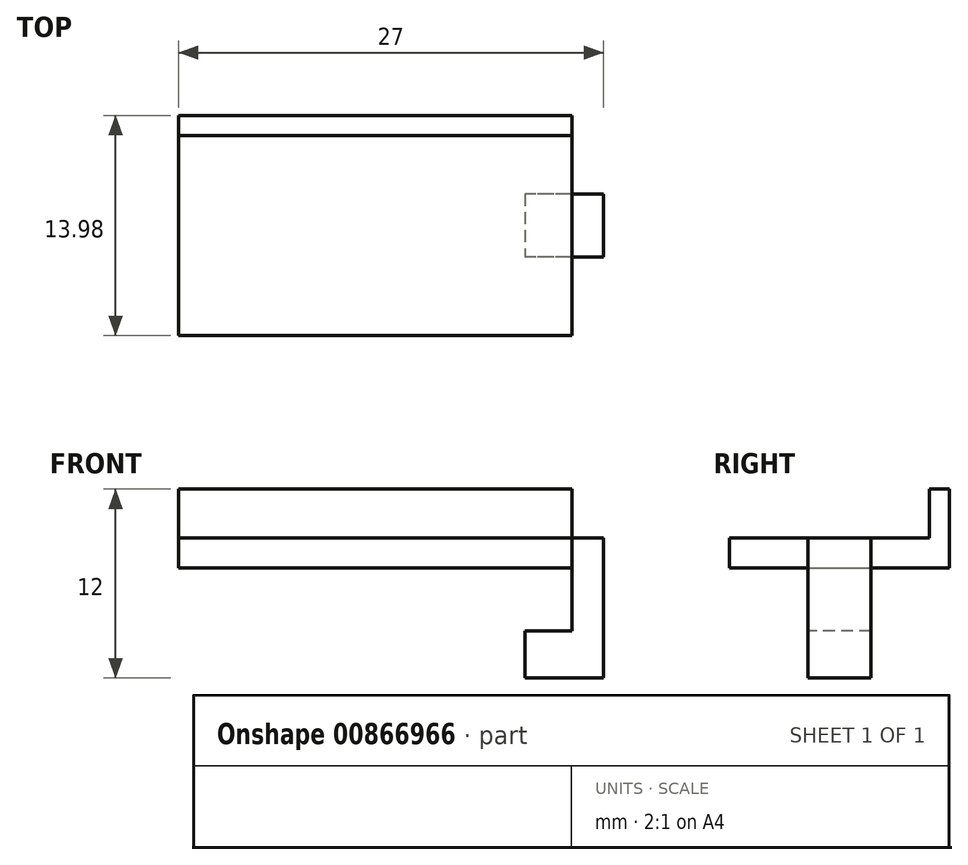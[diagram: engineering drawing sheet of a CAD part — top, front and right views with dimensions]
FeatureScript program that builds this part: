
annotation { "Feature Type Name" : "Feature", "Feature Type Description" : "" }
export const myFeature = defineFeature(function(context is Context, id is Id, definition is map)
    precondition{}
    {
        {
            var Q0;
            Q0=qCreatedBy(makeId("Top.planeOp"),FACE);
            var sketch = newSketch(context, id + "F0", { "sketchPlane" : qUnion([Q0])});
            skLineSegment(sketch, "E0.bottom", {"start": v(12.5, -6.99) * mm, "end": v(-12.5, -6.99) * mm});
            skLineSegment(sketch, "E0.top", {"start": v(12.5, 6.99) * mm, "end": v(-12.5, 6.99) * mm});
            skLineSegment(sketch, "E0.left", {"start": v(12.5, -6.99) * mm, "end": v(12.5, 6.98) * mm});
            skLineSegment(sketch, "E0.right", {"start": v(-12.5, -6.99) * mm, "end": v(-12.5, 6.98) * mm});
            skPoint(sketch, "E0.middle", {"position": v(0, 0) * mm});
            skLineSegment(sketch, "E1", {"start": v(-14, 6.99) * mm, "end": v(-14, 5.72) * mm});
            skLineSegment(sketch, "E2", {"start": v(-12.5, 5.72) * mm, "end": v(12.5, 5.72) * mm});
            skSolve(sketch);
        }
        {
            var Q0;
            {var subQ0=sQuery(id+"F0.wireOp",EDGE,"E0.bottom");Q0=makeQuery(id+"F0.imprint","IMPRINT",FACE,{"disambiguationData":[TD([[makeQuery(id+"F0.imprint","IMPRINT",EDGE,{"derivedFrom":subQ0}),-1.0]])]});}
            extrude(context, id + "F1", {"entities" : qUnion([Q0]), "depth" : 1.9 * mm, "offsetDistance" : 25 * mm});
        }
        {
            var Q0;
            {var subQ0=sQuery(id+"F0.wireOp",EDGE,"E0.top");Q0=makeQuery(id+"F0.imprint","IMPRINT",FACE,{"disambiguationData":[TD([[makeQuery(id+"F0.imprint","IMPRINT",EDGE,{"derivedFrom":subQ0}),1.0]])]});}
            extrude(context, id + "F2", {"entities" : qUnion([Q0]), "operationType" : NewBodyOperationType.ADD, "depth" : 5 * mm, "offsetDistance" : 25 * mm});
        }
        {
            var Q0;
            Q0=qCreatedBy(makeId("Right.planeOp"),FACE);
            var sketch = newSketch(context, id + "F3", { "sketchPlane" : qUnion([Q0])});
            skLineSegment(sketch, "E3", {"start": v(2, 0) * mm, "end": v(-2, 0) * mm});
            skLineSegment(sketch, "E4", {"start": v(2, 0) * mm, "end": v(2, -4) * mm});
            skLineSegment(sketch, "E5", {"start": v(2, -4) * mm, "end": v(-2, -4) * mm});
            skLineSegment(sketch, "E6", {"start": v(-2, -4) * mm, "end": v(-2, 0) * mm});
            skLineSegment(sketch, "E7", {"start": v(2, 0) * mm, "end": v(2, 1.9) * mm});
            skLineSegment(sketch, "E8", {"start": v(2, 1.9) * mm, "end": v(-2, 1.9) * mm});
            skLineSegment(sketch, "E9", {"start": v(-2, 1.9) * mm, "end": v(-2, 0) * mm});
            skLineSegment(sketch, "E10", {"start": v(2, -4) * mm, "end": v(2, -7) * mm});
            skLineSegment(sketch, "E11", {"start": v(2, -7) * mm, "end": v(-2, -7) * mm});
            skLineSegment(sketch, "E12", {"start": v(-2, -7) * mm, "end": v(-2, -4) * mm});
            skSolve(sketch);
        }
        {
            var Q0;
            Q0=makeQuery(id+"F3.imprint","IMPRINT",FACE,{"disambiguationData":[TD([[makeQuery(id+"F3.imprint","IMPRINT",EDGE,{"derivedFrom":sQuery(id+"F3.wireOp",EDGE,"E3")}),-1.0]])]});
            var Q1;
            Q1=makeQuery(id+"F3.imprint","IMPRINT",FACE,{"disambiguationData":[TD([[makeQuery(id+"F3.imprint","IMPRINT",EDGE,{"derivedFrom":sQuery(id+"F3.wireOp",EDGE,"E3")}),1.0]])]});
            extrude(context, id + "F4", {"entities" : qUnion([Q0, Q1]), "depth" : 14.5 * mm, "offsetDistance" : 25 * mm, "hasSecondDirection" : true, "secondDirectionOppositeDirection" : false, "secondDirectionDepth" : 12.5 * mm});
        }
        {
            var Q0;
            Q0=makeQuery(id+"F3.imprint","IMPRINT",FACE,{"disambiguationData":[TD([[makeQuery(id+"F3.imprint","IMPRINT",EDGE,{"derivedFrom":sQuery(id+"F3.wireOp",EDGE,"E5")}),1.0]])]});
            extrude(context, id + "F5", {"entities" : qUnion([Q0]), "operationType" : NewBodyOperationType.ADD, "depth" : 14.5 * mm, "offsetDistance" : 25 * mm, "hasSecondDirection" : true, "secondDirectionOppositeDirection" : false, "secondDirectionDepth" : 9.5 * mm});
        }
    });
